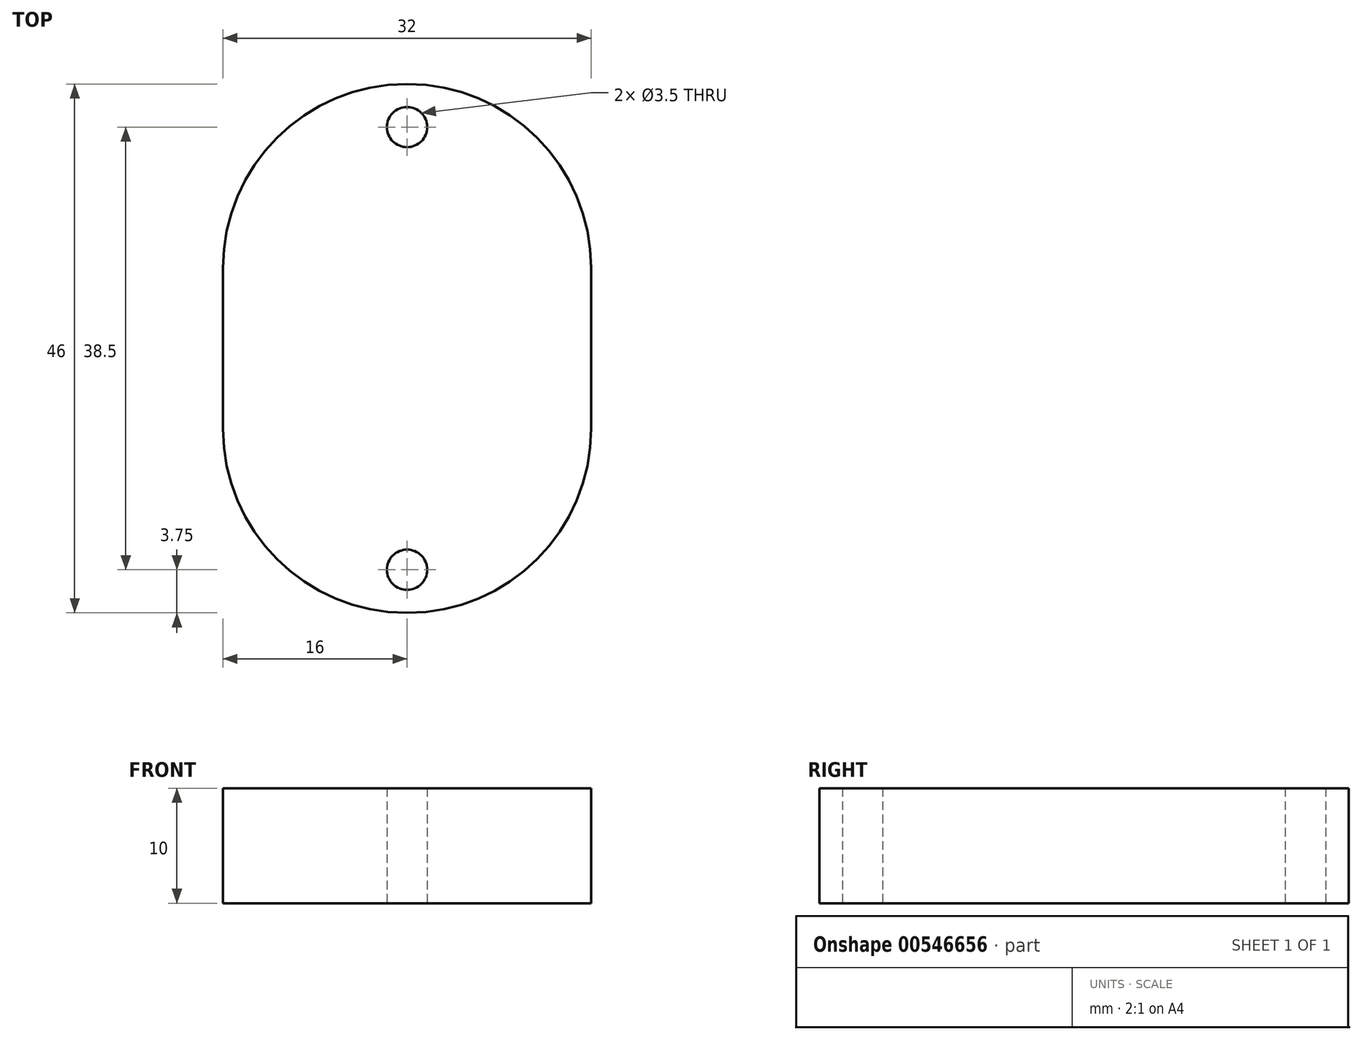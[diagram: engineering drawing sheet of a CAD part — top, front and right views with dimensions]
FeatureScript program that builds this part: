
annotation { "Feature Type Name" : "Feature", "Feature Type Description" : "" }
export const myFeature = defineFeature(function(context is Context, id is Id, definition is map)
    precondition{}
    {
        {
            var Q0;
            Q0=qCreatedBy(makeId("Top.planeOp"),FACE);
            var sketch = newSketch(context, id + "F0", { "sketchPlane" : qUnion([Q0])});
            skLineSegment(sketch, "E0.bottom", {"start": v(0, 23) * mm, "end": v(0, 23) * mm});
            skLineSegment(sketch, "E0.top", {"start": v(0, -23) * mm, "end": v(0, -23) * mm});
            skLineSegment(sketch, "E0.left", {"start": v(16, 7) * mm, "end": v(16, -7) * mm});
            skLineSegment(sketch, "E0.right", {"start": v(-16, 7) * mm, "end": v(-16, -7) * mm});
            skPoint(sketch, "E0.middle", {"position": v(0, 0) * mm});
            skCircle(sketch, "E1", {"center": v(0, 19.25) * mm, "radius": 1.75 * mm});
            skCircle(sketch, "E2.MirrorC", {"center": v(0, -19.25) * mm, "radius": 1.75 * mm});
            skPoint(sketch, "E3.visualSharp", {"position": v(-16, 23) * mm});
            skArc(sketch, "E3.filletArc", {"start": v(0, 23) * mm, "mid": v(-11.31, 18.31) * mm, "end": v(-16, 7) * mm});
            skPoint(sketch, "E4.visualSharp", {"position": v(16, 23) * mm});
            skArc(sketch, "E4.filletArc", {"start": v(16, 7) * mm, "mid": v(11.31, 18.31) * mm, "end": v(0, 23) * mm});
            skPoint(sketch, "E5.visualSharp", {"position": v(16, -23) * mm});
            skArc(sketch, "E5.filletArc", {"start": v(0, -23) * mm, "mid": v(11.31, -18.31) * mm, "end": v(16, -7) * mm});
            skPoint(sketch, "E6.visualSharp", {"position": v(-16, -23) * mm});
            skArc(sketch, "E6.filletArc", {"start": v(-16, -7) * mm, "mid": v(-11.31, -18.31) * mm, "end": v(0, -23) * mm});
            skSolve(sketch);
        }
        {
            var Q0;
            Q0 = qSketchRegion(id + "F0", true);
            extrude(context, id + "F1", {"entities" : qUnion([Q0]), "depth" : 10 * mm, "offsetDistance" : 25 * mm});
        }
    });
